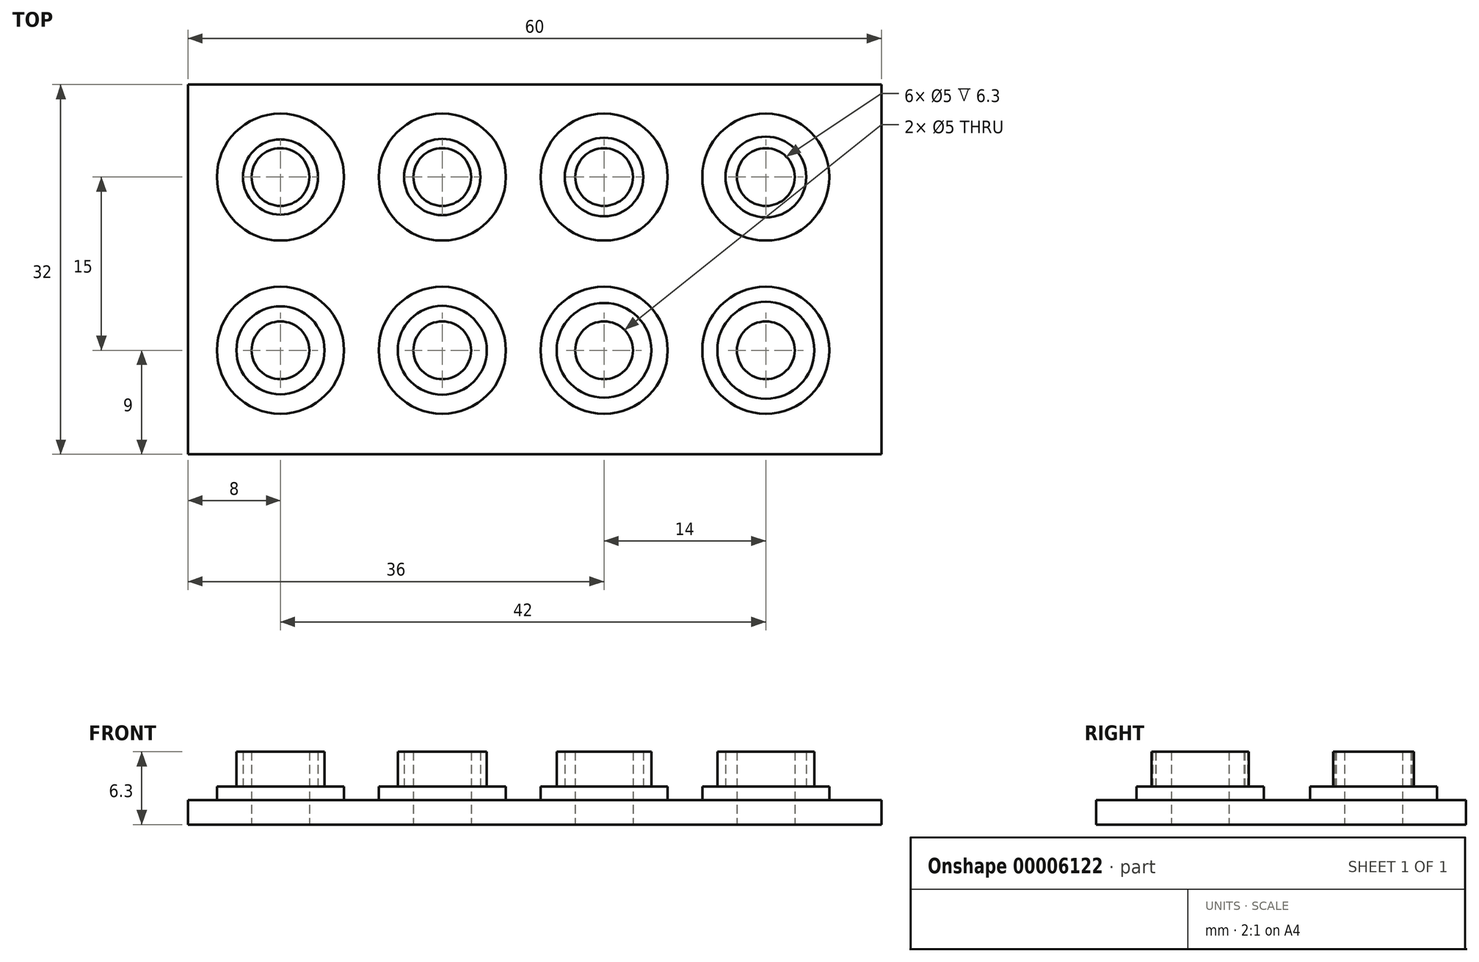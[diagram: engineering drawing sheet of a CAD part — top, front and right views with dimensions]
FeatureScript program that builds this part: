
annotation { "Feature Type Name" : "Feature", "Feature Type Description" : "" }
export const myFeature = defineFeature(function(context is Context, id is Id, definition is map)
    precondition{}
    {
        {
            var Q0;
            Q0=qCreatedBy(makeId("Top.planeOp"),FACE);
            var sketch = newSketch(context, id + "F0", { "sketchPlane" : qUnion([Q0])});
            skLineSegment(sketch, "E0.bottom", {"start": v(0, 0) * mm, "end": v(60, 0) * mm});
            skLineSegment(sketch, "E0.top", {"start": v(0, -32) * mm, "end": v(60, -32) * mm});
            skLineSegment(sketch, "E0.left", {"start": v(0, 0) * mm, "end": v(0, -32) * mm});
            skLineSegment(sketch, "E0.right", {"start": v(60, 0) * mm, "end": v(60, -32) * mm});
            skCircle(sketch, "E1", {"center": v(8, -8) * mm, "radius": 2.5 * mm});
            skCircle(sketch, "E2", {"center": v(22, -8) * mm, "radius": 2.5 * mm});
            skCircle(sketch, "E3", {"center": v(36, -8) * mm, "radius": 2.5 * mm});
            skCircle(sketch, "E4", {"center": v(50, -8) * mm, "radius": 2.5 * mm});
            skCircle(sketch, "E5", {"center": v(22, -23) * mm, "radius": 2.5 * mm});
            skCircle(sketch, "E6", {"center": v(50, -23) * mm, "radius": 2.5 * mm});
            skCircle(sketch, "E7", {"center": v(8, -23) * mm, "radius": 2.5 * mm});
            skCircle(sketch, "E8", {"center": v(36, -23) * mm, "radius": 2.5 * mm});
            skSolve(sketch);
        }
        {
            var Q0;
            Q0=makeQuery(id+"F0.imprint","IMPRINT",FACE,{"disambiguationData":[TD([[makeQuery(id+"F0.imprint","IMPRINT",EDGE,{"derivedFrom":sQuery(id+"F0.wireOp",EDGE,"E0.bottom")}),-1.0]])]});
            extrude(context, id + "F1", {"entities" : qUnion([Q0]), "depth" : 2.1 * mm});
        }
        {
            var Q0;
            Q0=makeQuery(id+"F1.opExtrude","CAP_FACE",FACE,{"disambiguationData":[OSD([sQuery(id+"F0.wireOp",EDGE,"E0.bottom"),sQuery(id+"F0.wireOp",EDGE,"E0.top"),sQuery(id+"F0.wireOp",EDGE,"E0.left"),sQuery(id+"F0.wireOp",EDGE,"E0.right"),sQuery(id+"F0.wireOp",EDGE,"E1"),sQuery(id+"F0.wireOp",EDGE,"E2"),sQuery(id+"F0.wireOp",EDGE,"E3"),sQuery(id+"F0.wireOp",EDGE,"E4"),sQuery(id+"F0.wireOp",EDGE,"E5"),sQuery(id+"F0.wireOp",EDGE,"E6"),sQuery(id+"F0.wireOp",EDGE,"E7"),sQuery(id+"F0.wireOp",EDGE,"E8")])],"isStart":false});
            var sketch = newSketch(context, id + "F2", { "sketchPlane" : qUnion([Q0])});
            skCircle(sketch, "E9", {"center": v(8, -8) * mm, "radius": 5.5 * mm});
            skCircle(sketch, "E10", {"center": v(8, -8) * mm, "radius": 2.5 * mm});
            skCircle(sketch, "E11", {"center": v(22, -8) * mm, "radius": 5.5 * mm});
            skCircle(sketch, "E12", {"center": v(22, -8) * mm, "radius": 2.5 * mm});
            skCircle(sketch, "E13", {"center": v(36, -8) * mm, "radius": 5.5 * mm});
            skCircle(sketch, "E14", {"center": v(36, -8) * mm, "radius": 2.5 * mm});
            skCircle(sketch, "E15", {"center": v(50, -8) * mm, "radius": 5.5 * mm});
            skCircle(sketch, "E16", {"center": v(50, -8) * mm, "radius": 2.5 * mm});
            skCircle(sketch, "E17", {"center": v(8, -23) * mm, "radius": 5.5 * mm});
            skCircle(sketch, "E18", {"center": v(8, -23) * mm, "radius": 2.5 * mm});
            skCircle(sketch, "E19", {"center": v(22, -23) * mm, "radius": 5.5 * mm});
            skCircle(sketch, "E20", {"center": v(22, -23) * mm, "radius": 2.5 * mm});
            skCircle(sketch, "E21", {"center": v(36, -23) * mm, "radius": 5.5 * mm});
            skCircle(sketch, "E22", {"center": v(36, -23) * mm, "radius": 2.5 * mm});
            skCircle(sketch, "E23", {"center": v(50, -23) * mm, "radius": 5.5 * mm});
            skCircle(sketch, "E24", {"center": v(50, -23) * mm, "radius": 2.5 * mm});
            skSolve(sketch);
        }
        {
            var Q0;
            Q0 = qSketchRegion(id + "F2", true);
            extrude(context, id + "F3", {"entities" : qUnion([Q0]), "operationType" : NewBodyOperationType.ADD, "depth" : 1.2 * mm});
        }
        {
            var Q0;
            Q0=makeQuery(id+"F3.opExtrude","CAP_FACE",FACE,{"disambiguationData":[OSD([sQuery(id+"F2.wireOp",EDGE,"E9"),sQuery(id+"F2.wireOp",EDGE,"E10")])],"isStart":false});
            cPlane(context, id + "F4", {"entities" : qUnion([Q0]), "cplaneType" : CPlaneType.OFFSET, "offset" : 0 * mm, "width" : 150 * mm, "height" : 150 * mm});
        }
        {
            var Q0;
            Q0=qCreatedBy(id+"F4.planeOp",FACE);
            var sketch = newSketch(context, id + "F5", { "sketchPlane" : qUnion([Q0])});
            skCircle(sketch, "E25", {"center": v(8, -8) * mm, "radius": 3.25 * mm});
            skCircle(sketch, "E26", {"center": v(8, -8) * mm, "radius": 2.5 * mm});
            skCircle(sketch, "E27", {"center": v(22, -8) * mm, "radius": 3.3 * mm});
            skCircle(sketch, "E28", {"center": v(22, -8) * mm, "radius": 2.5 * mm});
            skCircle(sketch, "E29", {"center": v(36, -8) * mm, "radius": 3.4 * mm});
            skCircle(sketch, "E30", {"center": v(36, -8) * mm, "radius": 2.5 * mm});
            skCircle(sketch, "E31", {"center": v(50, -8) * mm, "radius": 3.5 * mm});
            skCircle(sketch, "E32", {"center": v(50, -8) * mm, "radius": 2.5 * mm});
            skCircle(sketch, "E33", {"center": v(8, -23) * mm, "radius": 3.81 * mm});
            skCircle(sketch, "E34", {"center": v(8, -23) * mm, "radius": 2.5 * mm});
            skCircle(sketch, "E35", {"center": v(22, -23) * mm, "radius": 3.85 * mm});
            skCircle(sketch, "E36", {"center": v(22, -23) * mm, "radius": 2.5 * mm});
            skCircle(sketch, "E37", {"center": v(36, -23) * mm, "radius": 4.1 * mm});
            skCircle(sketch, "E38", {"center": v(36, -23) * mm, "radius": 2.5 * mm});
            skCircle(sketch, "E39", {"center": v(50, -23) * mm, "radius": 4.2 * mm});
            skCircle(sketch, "E40", {"center": v(50, -23) * mm, "radius": 2.5 * mm});
            skSolve(sketch);
        }
        {
            var Q0;
            Q0 = qSketchRegion(id + "F5", true);
            extrude(context, id + "F6", {"entities" : qUnion([Q0]), "operationType" : NewBodyOperationType.ADD, "depth" : 3 * mm});
        }
    });
